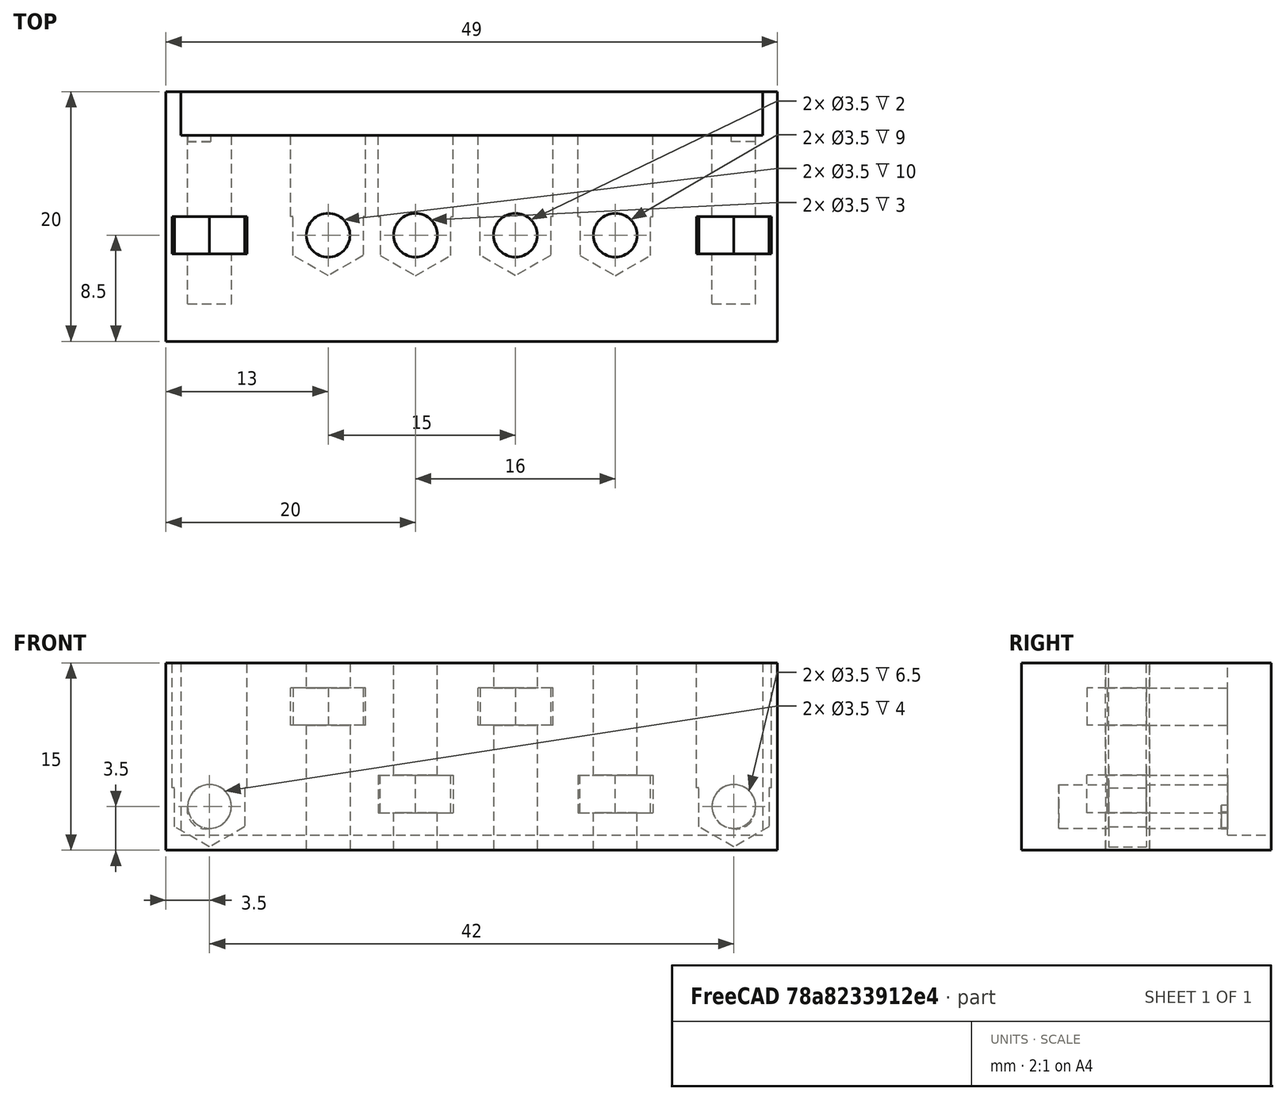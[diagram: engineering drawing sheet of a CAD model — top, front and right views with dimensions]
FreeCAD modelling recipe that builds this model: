
FCSTD DOCUMENT  (FreeCAD 0.19R14555 (Git shallow))
Label: Soporte Ultrasonidos
License: All rights reserved
LicenseURL: http://en.wikipedia.org/wiki/All_rights_reserved
objects: Part::MultiFuse×12, Part::Box×9, Part::Cylinder×8, Part::Prism×6, Part::Cut×3
note: 38 computed .brp shape members not serialized (recipe doc carries the construction recipe); baked Part::Feature solids carry a one-line shape summary decoded from their .brp

FEATURE [Part::Box] Box  label="Cubo"
  AttacherType = Attacher::AttachEngine3D
  Height = 15
  Length = 49
  Width = 5
FEATURE [Part::Box] Box001  label="Cubo001"
  AttacherType = Attacher::AttachEngine3D
  Height = 21
  Length = 46.6
  Placement = pos=(1.2,1.5,1.2) rot=(0,0,1;0rad)
  Width = 10
FEATURE [Part::Cut] Cut
  Base = -> Box
  Tool = -> Box001
FEATURE [Part::Cylinder] Cylinder  label="Cilindro"
  Angle = 360
  AttacherType = Attacher::AttachEngine3D
  Height = 10
  Placement = pos=(3.2,8,3.2) rot=(1,0,0;1.5708rad)
  Radius = 1.5
FEATURE [Part::Cylinder] Cylinder001  label="Cilindro001"
  Angle = 360
  AttacherType = Attacher::AttachEngine3D
  Height = 10
  Placement = pos=(45.7,8,3.2) rot=(1,0,0;1.5708rad)
  Radius = 1.5
FEATURE [Part::MultiFuse] Fusion
  Shapes = -> [Cylinder,Cylinder001]
FEATURE [Part::Cut] Cut001
  Base = -> Cut
  Tool = -> Fusion
FEATURE [Part::Cylinder] Cylinder004  label="Cilindro004"
  Angle = 360
  AttacherType = Attacher::AttachEngine3D
  Height = 20
  Placement = pos=(34,7.5,-1) rot=(0,0,1;0rad)
  Radius = 1.75
FEATURE [Part::Prism] Prism002  label="Prisma002"
  AttacherType = Attacher::AttachEngine3D
  Circumradius = 3.25
  FirstAngle = 0
  Height = 3
  Placement = pos=(34,7.5,3) rot=(0,0,1;1.5708rad)
  Polygon = 6
  SecondAngle = 0
FEATURE [Part::Box] Box003  label="Cubo003"
  AttacherType = Attacher::AttachEngine3D
  Height = 3
  Length = 6
  Placement = pos=(31,9,3) rot=(0,0,1;0rad)
  Width = 20
FEATURE [Part::MultiFuse] Fusion001
  Placement = pos=(47,-3,0) rot=(0,0,1;3.14159rad)
  Shapes = -> [Box003,Prism002,Cylinder004]
FEATURE [Part::Box] Box004  label="Cubo004"
  AttacherType = Attacher::AttachEngine3D
  Height = 15
  Length = 49
  Placement = pos=(0,-15,0) rot=(0,0,1;0rad)
  Width = 16
FEATURE [Part::Prism] Prism003  label="Prisma003"
  AttacherType = Attacher::AttachEngine3D
  Circumradius = 3.25
  FirstAngle = 0
  Height = 3
  Placement = pos=(34,7.5,3) rot=(0,0,1;1.5708rad)
  Polygon = 6
  SecondAngle = 0
FEATURE [Part::Cylinder] Cylinder005  label="Cilindro005"
  Angle = 360
  AttacherType = Attacher::AttachEngine3D
  Height = 20
  Placement = pos=(34,7.5,-1) rot=(0,0,1;0rad)
  Radius = 1.75
FEATURE [Part::Box] Box005  label="Cubo005"
  AttacherType = Attacher::AttachEngine3D
  Height = 3
  Length = 6
  Placement = pos=(31,9,3) rot=(0,0,1;0rad)
  Width = 20
FEATURE [Part::MultiFuse] Fusion002
  Placement = pos=(62,-3,0) rot=(0,0,1;3.14159rad)
  Shapes = -> [Box005,Prism003,Cylinder005]
FEATURE [Part::MultiFuse] Fusion003
  Shapes = -> [Fusion002,Fusion001]
FEATURE [Part::Prism] Prism004  label="Prisma004"
  AttacherType = Attacher::AttachEngine3D
  Circumradius = 3.25
  FirstAngle = 0
  Height = 3
  Placement = pos=(34,7.5,3) rot=(0,0,1;1.5708rad)
  Polygon = 6
  SecondAngle = 0
FEATURE [Part::Cylinder] Cylinder006  label="Cilindro006"
  Angle = 360
  AttacherType = Attacher::AttachEngine3D
  Height = 20
  Placement = pos=(34,7.5,-1) rot=(0,0,1;0rad)
  Radius = 1.75
FEATURE [Part::Box] Box006  label="Cubo006"
  AttacherType = Attacher::AttachEngine3D
  Height = 3
  Length = 6
  Placement = pos=(31,9,3) rot=(0,0,1;0rad)
  Width = 20
FEATURE [Part::MultiFuse] Fusion004
  Placement = pos=(-14,-3,16) rot=(1,0,0;3.14159rad)
  Shapes = -> [Box006,Prism004,Cylinder006]
FEATURE [Part::Box] Box007  label="Cubo007"
  AttacherType = Attacher::AttachEngine3D
  Height = 3
  Length = 6
  Placement = pos=(31,9,3) rot=(0,0,1;0rad)
  Width = 20
FEATURE [Part::Cylinder] Cylinder007  label="Cilindro007"
  Angle = 360
  AttacherType = Attacher::AttachEngine3D
  Height = 20
  Placement = pos=(34,7.5,-1) rot=(0,0,1;0rad)
  Radius = 1.75
FEATURE [Part::Prism] Prism005  label="Prisma005"
  AttacherType = Attacher::AttachEngine3D
  Circumradius = 3.25
  FirstAngle = 0
  Height = 3
  Placement = pos=(34,7.5,3) rot=(0,0,1;1.5708rad)
  Polygon = 6
  SecondAngle = 0
FEATURE [Part::MultiFuse] Fusion005
  Placement = pos=(2,-3,16) rot=(1,0,0;3.14159rad)
  Shapes = -> [Box007,Prism005,Cylinder007]
FEATURE [Part::MultiFuse] Fusion006
  Shapes = -> [Fusion005,Fusion004]
FEATURE [Part::MultiFuse] Fusion007
  Placement = pos=(0,-17,16) rot=(1,0,0;3.14159rad)
  Shapes = -> [Fusion003,Fusion006]
FEATURE [Part::Box] Box008  label="Cubo008"
  AttacherType = Attacher::AttachEngine3D
  Height = 3
  Length = 6
  Placement = pos=(31,9,3) rot=(0,0,1;0rad)
  Width = 20
FEATURE [Part::Cylinder] Cylinder008  label="Cilindro008"
  Angle = 360
  AttacherType = Attacher::AttachEngine3D
  Height = 20
  Placement = pos=(34,7.5,-1) rot=(0,0,1;0rad)
  Radius = 1.75
FEATURE [Part::Prism] Prism006  label="Prisma006"
  AttacherType = Attacher::AttachEngine3D
  Circumradius = 3.25
  FirstAngle = 0
  Height = 3
  Placement = pos=(34,7.5,3) rot=(0,0,1;1.5708rad)
  Polygon = 6
  SecondAngle = 0
FEATURE [Part::MultiFuse] Fusion008
  Placement = pos=(37.5,-11,-4) rot=(0,-0.707107,-0.707107;3.14159rad)
  Shapes = -> [Box008,Prism006,Cylinder008]
FEATURE [Part::Box] Box009  label="Cubo009"
  AttacherType = Attacher::AttachEngine3D
  Height = 3
  Length = 6
  Placement = pos=(31,9,3) rot=(0,0,1;0rad)
  Width = 20
FEATURE [Part::Cylinder] Cylinder009  label="Cilindro009"
  Angle = 360
  AttacherType = Attacher::AttachEngine3D
  Height = 20
  Placement = pos=(34,7.5,-1) rot=(0,0,1;0rad)
  Radius = 1.75
FEATURE [Part::Prism] Prism007  label="Prisma007"
  AttacherType = Attacher::AttachEngine3D
  Circumradius = 3.25
  FirstAngle = 0
  Height = 3
  Placement = pos=(34,7.5,3) rot=(0,0,1;1.5708rad)
  Polygon = 6
  SecondAngle = 0
FEATURE [Part::MultiFuse] Fusion009
  Placement = pos=(79.5,-11,-4) rot=(0,0.707107,0.707107;3.14159rad)
  Shapes = -> [Box009,Prism007,Cylinder009]
FEATURE [Part::MultiFuse] Fusion010
  Shapes = -> [Box004,Cut001]
FEATURE [Part::MultiFuse] Fusion011
  Shapes = -> [Fusion009,Fusion007,Fusion008]
FEATURE [Part::Cut] Cut002
  Base = -> Fusion010
  Tool = -> Fusion011
